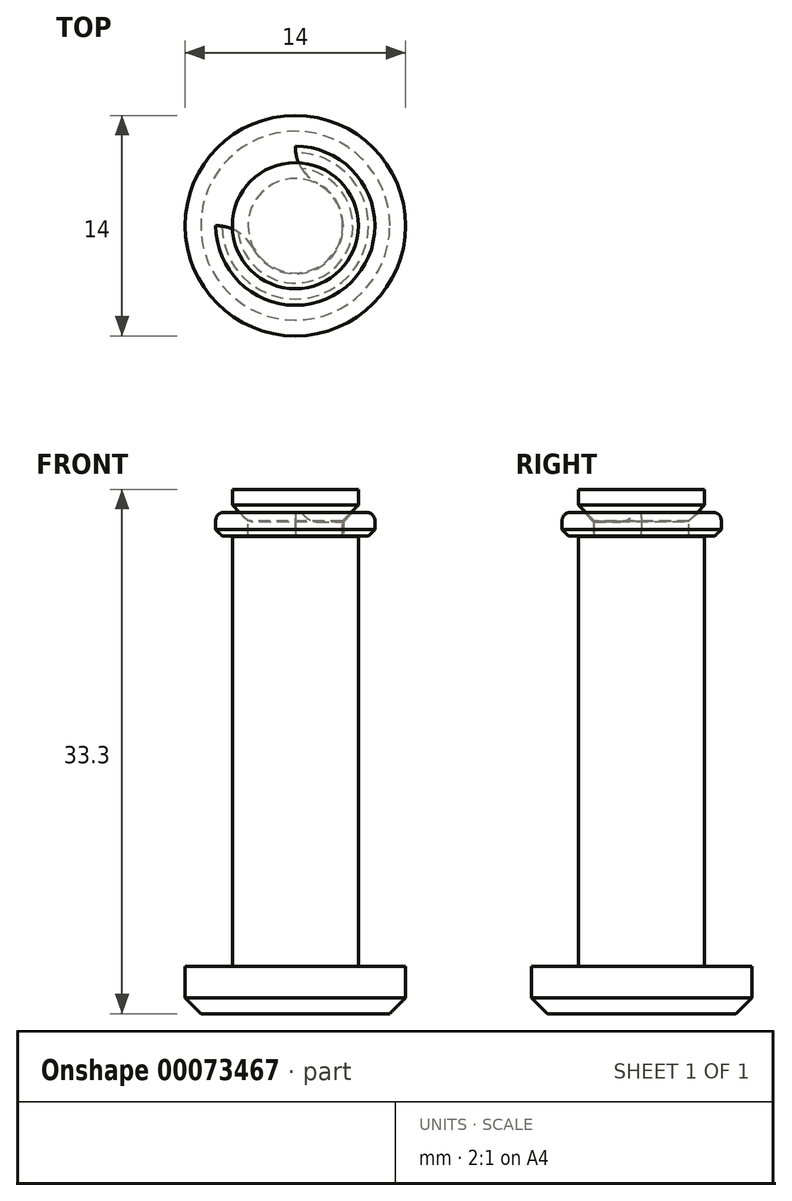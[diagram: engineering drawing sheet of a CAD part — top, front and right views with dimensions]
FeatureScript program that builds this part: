
annotation { "Feature Type Name" : "Feature", "Feature Type Description" : "" }
export const myFeature = defineFeature(function(context is Context, id is Id, definition is map)
    precondition{}
    {
        {
            var Q0;
            Q0=qCreatedBy(makeId("Top.planeOp"),FACE);
            var sketch = newSketch(context, id + "F0", { "sketchPlane" : qUnion([Q0])});
            skCircle(sketch, "E0", {"center": v(0, 0) * mm, "radius": 4 * mm});
            skSolve(sketch);
        }
        {
            var Q0;
            Q0 = qSketchRegion(id + "F0", true);
            extrude(context, id + "F1", {"entities" : qUnion([Q0]), "depth" : 30.3 * mm});
        }
        {
            var Q0;
            Q0=qCreatedBy(makeId("Top.planeOp"),FACE);
            var sketch = newSketch(context, id + "F2", { "sketchPlane" : qUnion([Q0])});
            skCircle(sketch, "E1", {"center": v(0, 0) * mm, "radius": 7 * mm});
            skSolve(sketch);
        }
        {
            var Q0;
            Q0 = qSketchRegion(id + "F2", true);
            extrude(context, id + "F3", {"entities" : qUnion([Q0]), "operationType" : NewBodyOperationType.ADD, "oppositeDirection" : true, "depth" : 3 * mm});
        }
        {
            var Q0;
            Q0=qCreatedBy(makeId("Front.planeOp"),FACE);
            var sketch = newSketch(context, id + "F4", { "sketchPlane" : qUnion([Q0])});
            skLineSegment(sketch, "E2", {"start": v(-4.1, 29.3) * mm, "end": v(-4.1, 27.3) * mm});
            skLineSegment(sketch, "E3", {"start": v(-4.1, 27.3) * mm, "end": v(-3, 27.3) * mm});
            skLineSegment(sketch, "E4", {"start": v(-3, 27.3) * mm, "end": v(-3, 28.3) * mm});
            skLineSegment(sketch, "E5", {"start": v(-3, 28.3) * mm, "end": v(-4, 29.3) * mm});
            skLineSegment(sketch, "E6", {"start": v(-4, 29.3) * mm, "end": v(-4.1, 29.3) * mm});
            skLineSegment(sketch, "E7", {"start": v(0, 30.3) * mm, "end": v(0, 29.3) * mm, "construction": true});
            skLineSegment(sketch, "E8", {"start": v(-4.1, 29.3) * mm, "end": v(0, 29.3) * mm, "construction": true});
            skSolve(sketch);
        }
        {
            var Q0;
            Q0 = qSketchRegion(id + "F4", true);
            var Q1;
            Q1=makeQuery(id+"F1.opExtrude","CAP_EDGE",EDGE,{"disambiguationData":[OSD([sQuery(id+"F0.wireOp",EDGE,"E0")])],"isStart":false});
            revolve(context, id + "F5", {"operationType" : NewBodyOperationType.REMOVE, "entities" : qUnion([Q0]), "axis" : qUnion([Q1]), "revolveType" : RevolveType.FULL, "oppositeDirection" : true});
        }
        {
            var Q0;
            Q0=makeQuery(id+"F3.opExtrude","CAP_EDGE",EDGE,{"disambiguationData":[OSD([sQuery(id+"F2.wireOp",EDGE,"E1")])],"isStart":false});
            chamfer(context, id + "F6", {"entities" : qUnion([Q0]), "width" : 1 * mm, "tangentPropagation" : true});
        }
        {
            var Q0;
            Q0=qCreatedBy(makeId("Front.planeOp"),FACE);
            var sketch = newSketch(context, id + "F7", { "sketchPlane" : qUnion([Q0])});
            skLineSegment(sketch, "E9", {"start": v(-5.05, 27.34) * mm, "end": v(-3.05, 27.34) * mm});
            skLineSegment(sketch, "E10", {"start": v(-3.05, 27.34) * mm, "end": v(-3.05, 28.24) * mm});
            skLineSegment(sketch, "E11", {"start": v(-3.05, 28.24) * mm, "end": v(-3.65, 28.84) * mm});
            skLineSegment(sketch, "E12", {"start": v(-5.05, 28.84) * mm, "end": v(-5.05, 27.34) * mm});
            skLineSegment(sketch, "E13", {"start": v(-3.65, 28.84) * mm, "end": v(-5.05, 28.84) * mm});
            skSolve(sketch);
        }
        {
            var Q0;
            Q0 = qSketchRegion(id + "F7", true);
            var Q1;
            Q1=makeQuery(id+"F1.opExtrude","CAP_EDGE",EDGE,{"disambiguationData":[OSD([sQuery(id+"F0.wireOp",EDGE,"E0")])],"isStart":false});
            revolve(context, id + "F8", {"entities" : qUnion([Q0]), "axis" : qUnion([Q1]), "revolveType" : RevolveType.ONE_DIRECTION, "angle" : 270 * degree});
        }
        {
            var Q0;
            Q0=makeQuery(id+"F8.opRevolve","CAP_EDGE",EDGE,{"disambiguationData":[OSD([sQuery(id+"F7.wireOp",EDGE,"E10")])],"isStart":false});
            var Q1;
            Q1=makeQuery(id+"F8.opRevolve","CAP_EDGE",EDGE,{"disambiguationData":[OSD([sQuery(id+"F7.wireOp",EDGE,"E10")])],"isStart":true});
            fillet(context, id + "F9", {"entities" : qUnion([Q0, Q1]), "radius" : 2.6 * mm, "tangentPropagation" : true, "allowEdgeOverflow" : false});
        }
        {
            var Q0;
            Q0=makeQuery(id+"F8.opRevolve","SWEPT_EDGE",EDGE,{"disambiguationData":[OSD([sQuery(id+"F7.wireOp",EDGE,"E12"),sQuery(id+"F7.wireOp",EDGE,"E13")])]});
            fillet(context, id + "F10", {"entities" : qUnion([Q0]), "radius" : .5 * mm, "tangentPropagation" : true, "allowEdgeOverflow" : false});
        }
        {
            var Q0;
            Q0=makeQuery(id+"F8.opRevolve","SWEPT_EDGE",EDGE,{"disambiguationData":[OSD([sQuery(id+"F7.wireOp",EDGE,"E9"),sQuery(id+"F7.wireOp",EDGE,"E12")])]});
            chamfer(context, id + "F11", {"entities" : qUnion([Q0]), "width" : .4 * mm, "tangentPropagation" : true});
        }
    });
